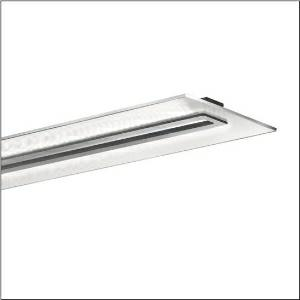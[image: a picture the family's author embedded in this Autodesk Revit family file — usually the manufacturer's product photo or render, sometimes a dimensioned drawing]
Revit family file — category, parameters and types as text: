
# Revit family: vega_r__11_5mn238dlc_e876
name_source: partatom
category: Lighting Fixtures
units: mm (PartAtom-declared; Revit-internal decimal feet)

## family parameters
Cut with Voids When Loaded = No
Host = Face
Light Source = No
Part Type = Normal
Room Calculation Point = No
Round Connector Dimension = Use Diameter
Shared = No

## types (1)
- --- (1 x LED 4000K / CRI = 80, 4300 lm, 31 W, 4000K)
    Apparent Load = 31 VA
    CIE Flux Codes = 61 86 97 62 100
    Color Rendering = 83
    Color Temperature = 4000K
    Default Elevation = 1800 mm
    Description = Vega® 11, office luminaire, primary light control with prismatic reflector, of PMMA, transparent prismatic structure, CAT 2 (L<= 1500cd/m²), light emission: direct/indirect distribution, primary light characteristic: symmetric, installation type: suspended mounting, surface-mounted, LED rated luminous flux: 4.300 lm, light colour: 840, colour temperature: 4000K, control gear: ECG, with terminal, 3+2-pole, max. 2.5mm², mains connection: 230V, AC, 50Hz, connection cable inclusive, cable length: 1,5 m, rated input power: 31W, luminaire housing, rectangular, rounded, of aluminium section, anodised, metallic grey (RAL 9006), length: 1.250 mm, width: 350 mm, height: 43mm, luminaire housing, lower part, of aluminium section, anodised, metallic grey (RAL 9006), of PC, grey, protection rating (complete): IP20, insulation class (complete): insulation class I (protective earthing), certification: CE, standard: EN 50419, packaging unit: 1 piece
    Height = 40 mm  [stored 0.131234 ft]
    Lamp = 1 x LED 4000K / CRI >= 80
    Lamp Light Flux = 4300 lm
    Lamp Power = 31 W
    Lamp count = 1
    Length = 1250 mm
    Luminous efficacy = 139 lm/W
    Manufacturer = Siteco
    ModVariant = No
    Model = 5MN238DLC
    Mounting Place = Ceiling
    Mounting Type = Pendant
    Number of Poles = 1
    OnlyDefault = Yes
    Power Factor = 1
    Product Name = Vega® 11
    Product group = office luminaire | ceiling pendant
    ProductGroupID = 905
    Protection Class = Protection class I
    Protection Degree = IP 20
    RLX_Detail_Level = 1
    RlxData = <blob elided: 63177 chars, md5=1416c2bf>
    Socket = socket
    Standby Power = 0 W
    System Light Flux = 4300 lm
    System Power = 31 W
    Type Comments = factory setting: luminous flux: 100 % | dim-lin: 254 | 231 mA
    Type Image = l_1004807.jpg
    URL = http://relux.com
    VarID = @adj_147129
    Voltage = 0 V
    Weight = 0.00 kg
    Width = 350 mm

note: [stored X ft] marks values corroborated as IEEE doubles in the binary element streams (Revit-internal decimal feet)

## geometry (parser evidence)
native form markers: Blend x4, Sweep x11
no freeform markers — native parametric forms only
